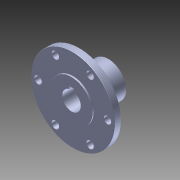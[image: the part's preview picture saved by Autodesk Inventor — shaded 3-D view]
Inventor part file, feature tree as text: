
AUTODESK INVENTOR PART (.ipt)
format: ipt  version: 2014 (Build 180170000, 170)  size: 156,160 bytes
history: native  units: in
note: dims shown in document units (in); Inventor stores cm internally (conversion verified against a paired STEP export)
features: other x2, chamfer x1
ambient origin geometry x8: Origin, YZ Plane, XZ Plane, XY Plane, X Axis, Y Axis, Z Axis, Center Point
bodies: Solid1 (feature_tree)
feature tree (3):
  other  "am-0077a-500 Key Hub r2.ipt"
  chamfer  "Chamfer2::am-0077a-500 Key Hub r2.ipt"  Distance=0.3937in
  other  "TaggingFeature1"
